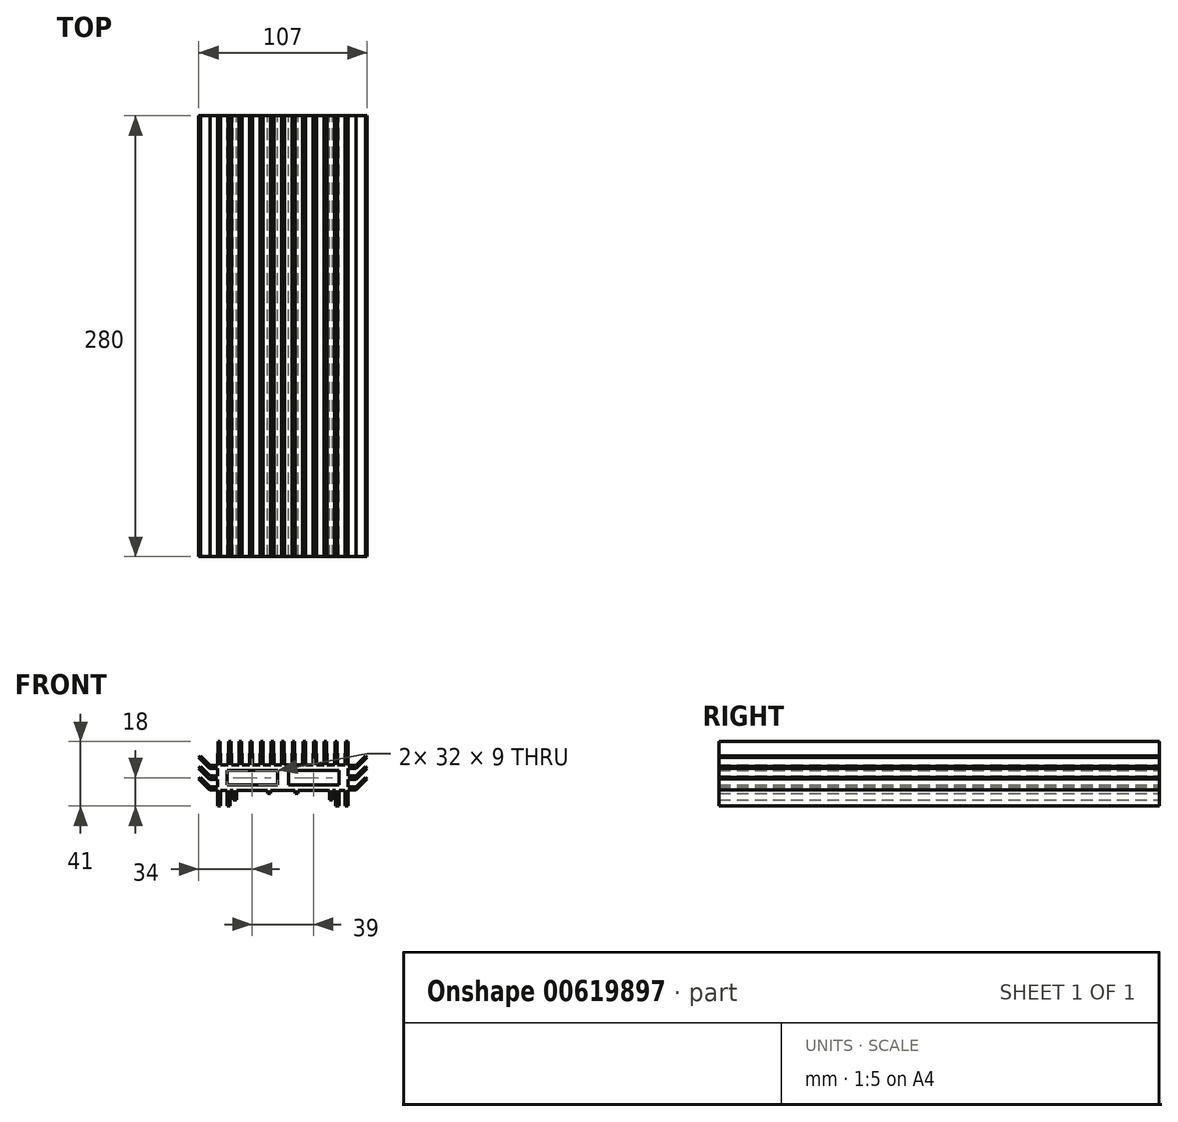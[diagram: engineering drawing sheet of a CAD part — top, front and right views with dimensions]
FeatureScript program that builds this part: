
annotation { "Feature Type Name" : "Feature", "Feature Type Description" : "" }
export const myFeature = defineFeature(function(context is Context, id is Id, definition is map)
    precondition{}
    {
        {
            var Q0;
            Q0=qCreatedBy(makeId("Front.planeOp"),FACE);
            var sketch = newSketch(context, id + "F0", { "sketchPlane" : qUnion([Q0])});
            skLineSegment(sketch, "E0", {"start": v(-39.5, -22.5) * mm, "end": v(-41.5, -22.5) * mm});
            skLineSegment(sketch, "E1", {"start": v(0, -12.5) * mm, "end": v(-7.75, -12.5) * mm});
            skLineSegment(sketch, "E2", {"start": v(-29.5, -12.5) * mm, "end": v(-29.5, -18.5) * mm});
            skLineSegment(sketch, "E3", {"start": v(-29.5, -18.5) * mm, "end": v(-31.5, -18.5) * mm});
            skLineSegment(sketch, "E4", {"start": v(-31.5, -18.5) * mm, "end": v(-31.5, -12.5) * mm});
            skLineSegment(sketch, "E5", {"start": v(-31.5, -12.5) * mm, "end": v(-33.5, -12.5) * mm});
            skLineSegment(sketch, "E6", {"start": v(-33.5, -12.5) * mm, "end": v(-33.5, -22.5) * mm});
            skLineSegment(sketch, "E7", {"start": v(-33.5, -22.5) * mm, "end": v(-35.5, -22.5) * mm});
            skLineSegment(sketch, "E8", {"start": v(-35.5, -22.5) * mm, "end": v(-35.5, -12.5) * mm});
            skLineSegment(sketch, "E9", {"start": v(-35.5, -12.5) * mm, "end": v(-39.5, -12.5) * mm});
            skLineSegment(sketch, "E10", {"start": v(-39.5, -12.5) * mm, "end": v(-39.5, -22.5) * mm});
            skLineSegment(sketch, "E11", {"start": v(-39.75, 18.5) * mm, "end": v(-39.5, 3.5) * mm});
            skLineSegment(sketch, "E12", {"start": v(-9.75, -12.5) * mm, "end": v(-9.75, -14.5) * mm});
            skLineSegment(sketch, "E13", {"start": v(-9.75, -14.5) * mm, "end": v(-7.75, -14.5) * mm});
            skLineSegment(sketch, "E14", {"start": v(-7.75, -14.5) * mm, "end": v(-7.75, -12.5) * mm});
            skLineSegment(sketch, "E15.trimOffspring", {"start": v(-9.75, -12.5) * mm, "end": v(-29.5, -12.5) * mm});
            skLineSegment(sketch, "E16", {"start": v(-39.5, 3.5) * mm, "end": v(-34.75, 3.5) * mm});
            skLineSegment(sketch, "E17", {"start": v(-41.5, 3.5) * mm, "end": v(-41.25, 18.5) * mm});
            skLineSegment(sketch, "E18", {"start": v(-41.25, 18.5) * mm, "end": v(-39.75, 18.5) * mm});
            skLineSegment(sketch, "E19", {"start": v(-41.5, 3.5) * mm, "end": v(-41.5, -22.5) * mm});
            skLineSegment(sketch, "E20.1.0.0", {"start": v(-33, 18.5) * mm, "end": v(-32.75, 3.5) * mm});
            skLineSegment(sketch, "E20.1.0.1", {"start": v(-32.75, 3.5) * mm, "end": v(-28, 3.5) * mm});
            skLineSegment(sketch, "E20.1.0.2", {"start": v(-34.75, 3.5) * mm, "end": v(-34.5, 18.5) * mm});
            skLineSegment(sketch, "E20.1.0.3", {"start": v(-34.5, 18.5) * mm, "end": v(-33, 18.5) * mm});
            skLineSegment(sketch, "E20.2.0.0", {"start": v(-26.25, 18.5) * mm, "end": v(-26, 3.5) * mm});
            skLineSegment(sketch, "E20.2.0.1", {"start": v(-26, 3.5) * mm, "end": v(-21.25, 3.5) * mm});
            skLineSegment(sketch, "E20.2.0.2", {"start": v(-28, 3.5) * mm, "end": v(-27.75, 18.5) * mm});
            skLineSegment(sketch, "E20.2.0.3", {"start": v(-27.75, 18.5) * mm, "end": v(-26.25, 18.5) * mm});
            skLineSegment(sketch, "E20.3.0.0", {"start": v(-19.5, 18.5) * mm, "end": v(-19.25, 3.5) * mm});
            skLineSegment(sketch, "E20.3.0.1", {"start": v(-19.25, 3.5) * mm, "end": v(-14.5, 3.5) * mm});
            skLineSegment(sketch, "E20.3.0.2", {"start": v(-21.25, 3.5) * mm, "end": v(-21, 18.5) * mm});
            skLineSegment(sketch, "E20.3.0.3", {"start": v(-21, 18.5) * mm, "end": v(-19.5, 18.5) * mm});
            skLineSegment(sketch, "E20.4.0.0", {"start": v(-12.75, 18.5) * mm, "end": v(-12.5, 3.5) * mm});
            skLineSegment(sketch, "E20.4.0.1", {"start": v(-12.5, 3.5) * mm, "end": v(-7.75, 3.5) * mm});
            skLineSegment(sketch, "E20.4.0.2", {"start": v(-14.5, 3.5) * mm, "end": v(-14.25, 18.5) * mm});
            skLineSegment(sketch, "E20.4.0.3", {"start": v(-14.25, 18.5) * mm, "end": v(-12.75, 18.5) * mm});
            skLineSegment(sketch, "E20.5.0.0", {"start": v(-6, 18.5) * mm, "end": v(-5.75, 3.5) * mm});
            skLineSegment(sketch, "E20.5.0.1", {"start": v(-5.75, 3.5) * mm, "end": v(-1, 3.5) * mm});
            skLineSegment(sketch, "E20.5.0.2", {"start": v(-7.75, 3.5) * mm, "end": v(-7.5, 18.5) * mm});
            skLineSegment(sketch, "E20.5.0.3", {"start": v(-7.5, 18.5) * mm, "end": v(-6, 18.5) * mm});
            skLineSegment(sketch, "E21.6.6.0", {"start": v(-1, 3.5) * mm, "end": v(-0.75, 18.5) * mm});
            skLineSegment(sketch, "E21.9.6.0", {"start": v(-0.75, 18.5) * mm, "end": v(0, 18.5) * mm});
            skPoint(sketch, "E22", {"position": v(0, 18.5) * mm});
            skLineSegment(sketch, "E23", {"start": v(0, 18.5) * mm, "end": v(0, -12.5) * mm});
            skLineSegment(sketch, "E24", {"start": v(-35.5, 0) * mm, "end": v(-3.5, 0) * mm});
            skLineSegment(sketch, "E25", {"start": v(-3.5, 0) * mm, "end": v(-3.5, -9) * mm});
            skLineSegment(sketch, "E26", {"start": v(-3.5, -9) * mm, "end": v(-35.5, -9) * mm});
            skLineSegment(sketch, "E27", {"start": v(-35.5, -9) * mm, "end": v(-35.5, 0) * mm});
            skSolve(sketch);
        }
        {
            var Q0;
            Q0 = qSketchRegion(id + "F0", true);
            extrude(context, id + "F1", {"entities" : qUnion([Q0]), "depth" : 280 * mm, "offsetDistance" : 25 * mm});
        }
        {
            var Q0;
            Q0=qCreatedBy(makeId("Front.planeOp"),FACE);
            var sketch = newSketch(context, id + "F2", { "sketchPlane" : qUnion([Q0])});
            skLineSegment(sketch, "E28", {"start": v(-41.5, -12.2) * mm, "end": v(-46.5, -12.2) * mm});
            skLineSegment(sketch, "E29", {"start": v(-46.5, -12.2) * mm, "end": v(-53.5, -5.2) * mm});
            skLineSegment(sketch, "E30", {"start": v(-53.5, -5.2) * mm, "end": v(-52.44, -4.13) * mm});
            skLineSegment(sketch, "E31", {"start": v(-52.44, -4.13) * mm, "end": v(-46.38, -10.2) * mm});
            skLineSegment(sketch, "E32", {"start": v(-46.38, -10.2) * mm, "end": v(-41.5, -10.2) * mm});
            skLineSegment(sketch, "E33", {"start": v(-41.5, -12.2) * mm, "end": v(-41.5, -10.2) * mm});
            skLineSegment(sketch, "E34.0.1.0", {"start": v(-46.5, -5.44) * mm, "end": v(-53.5, 1.56) * mm});
            skLineSegment(sketch, "E34.0.1.1", {"start": v(-41.5, -5.44) * mm, "end": v(-46.5, -5.44) * mm});
            skLineSegment(sketch, "E34.0.1.2", {"start": v(-46.38, -3.44) * mm, "end": v(-41.5, -3.44) * mm});
            skLineSegment(sketch, "E34.0.1.3", {"start": v(-41.5, -5.44) * mm, "end": v(-41.5, -3.44) * mm});
            skLineSegment(sketch, "E34.0.1.4", {"start": v(-52.44, 2.62) * mm, "end": v(-46.38, -3.44) * mm});
            skLineSegment(sketch, "E34.0.1.5", {"start": v(-53.5, 1.56) * mm, "end": v(-52.44, 2.62) * mm});
            skLineSegment(sketch, "E34.0.2.0", {"start": v(-46.5, 1.3) * mm, "end": v(-53.5, 8.3) * mm});
            skLineSegment(sketch, "E34.0.2.1", {"start": v(-41.5, 1.3) * mm, "end": v(-46.5, 1.3) * mm});
            skLineSegment(sketch, "E34.0.2.2", {"start": v(-46.38, 3.3) * mm, "end": v(-41.5, 3.3) * mm});
            skLineSegment(sketch, "E34.0.2.3", {"start": v(-41.5, 1.3) * mm, "end": v(-41.5, 3.3) * mm});
            skLineSegment(sketch, "E34.0.2.4", {"start": v(-52.44, 9.37) * mm, "end": v(-46.38, 3.3) * mm});
            skLineSegment(sketch, "E34.0.2.5", {"start": v(-53.5, 8.3) * mm, "end": v(-52.44, 9.37) * mm});
            skLineSegment(sketch, "E34.direction1", {"start": v(-46.5, -12.2) * mm, "end": v(-22.16, -12.2) * mm, "construction": true});
            skLineSegment(sketch, "E34.direction2", {"start": v(-46.5, -12.2) * mm, "end": v(-46.5, -5.44) * mm, "construction": true});
            skSolve(sketch);
        }
        {
            var Q0;
            Q0 = qSketchRegion(id + "F2", true);
            extrude(context, id + "F3", {"entities" : qUnion([Q0]), "operationType" : NewBodyOperationType.ADD, "depth" : 280 * mm, "offsetDistance" : 25 * mm});
        }
        {
            var Q0;
            Q0=makeQuery(id+"F1.opExtrude","SWEPT_BODY",BODY,{"disambiguationData":[OSD([sQuery(id+"F0.wireOp",EDGE,"E0"),sQuery(id+"F0.wireOp",EDGE,"E1"),sQuery(id+"F0.wireOp",EDGE,"E2"),sQuery(id+"F0.wireOp",EDGE,"E3"),sQuery(id+"F0.wireOp",EDGE,"E4"),sQuery(id+"F0.wireOp",EDGE,"E5"),sQuery(id+"F0.wireOp",EDGE,"E6"),sQuery(id+"F0.wireOp",EDGE,"E7"),sQuery(id+"F0.wireOp",EDGE,"E8"),sQuery(id+"F0.wireOp",EDGE,"E9"),sQuery(id+"F0.wireOp",EDGE,"E10"),sQuery(id+"F0.wireOp",EDGE,"E11"),sQuery(id+"F0.wireOp",EDGE,"E12"),sQuery(id+"F0.wireOp",EDGE,"E13"),sQuery(id+"F0.wireOp",EDGE,"E14"),sQuery(id+"F0.wireOp",EDGE,"E15.trimOffspring"),sQuery(id+"F0.wireOp",EDGE,"E16"),sQuery(id+"F0.wireOp",EDGE,"E17"),sQuery(id+"F0.wireOp",EDGE,"E18"),sQuery(id+"F0.wireOp",EDGE,"E19"),sQuery(id+"F0.wireOp",EDGE,"E20.1.0.0"),sQuery(id+"F0.wireOp",EDGE,"E20.1.0.1"),sQuery(id+"F0.wireOp",EDGE,"E20.1.0.2"),sQuery(id+"F0.wireOp",EDGE,"E20.1.0.3"),sQuery(id+"F0.wireOp",EDGE,"E20.2.0.0"),sQuery(id+"F0.wireOp",EDGE,"E20.2.0.1"),sQuery(id+"F0.wireOp",EDGE,"E20.2.0.2"),sQuery(id+"F0.wireOp",EDGE,"E20.2.0.3"),sQuery(id+"F0.wireOp",EDGE,"E20.3.0.0"),sQuery(id+"F0.wireOp",EDGE,"E20.3.0.1"),sQuery(id+"F0.wireOp",EDGE,"E20.3.0.2"),sQuery(id+"F0.wireOp",EDGE,"E20.3.0.3"),sQuery(id+"F0.wireOp",EDGE,"E20.4.0.0"),sQuery(id+"F0.wireOp",EDGE,"E20.4.0.1"),sQuery(id+"F0.wireOp",EDGE,"E20.4.0.2"),sQuery(id+"F0.wireOp",EDGE,"E20.4.0.3"),sQuery(id+"F0.wireOp",EDGE,"E20.5.0.0"),sQuery(id+"F0.wireOp",EDGE,"E20.5.0.1"),sQuery(id+"F0.wireOp",EDGE,"E20.5.0.2"),sQuery(id+"F0.wireOp",EDGE,"E20.5.0.3"),sQuery(id+"F0.wireOp",EDGE,"E21.6.6.0"),sQuery(id+"F0.wireOp",EDGE,"E21.9.6.0"),sQuery(id+"F0.wireOp",EDGE,"E23"),sQuery(id+"F0.wireOp",EDGE,"E24"),sQuery(id+"F0.wireOp",EDGE,"E25"),sQuery(id+"F0.wireOp",EDGE,"E26"),sQuery(id+"F0.wireOp",EDGE,"E27")])]});
            var Q1;
            Q1=makeQuery(id+"F1.opExtrude","SWEPT_FACE",FACE,{"disambiguationData":[OSD([sQuery(id+"F0.wireOp",EDGE,"E23")])]});
            mirror(context, id + "F4", {"operationType" : NewBodyOperationType.ADD, "entities" : qUnion([Q0]), "mirrorPlane" : qUnion([Q1])});
        }
    });
